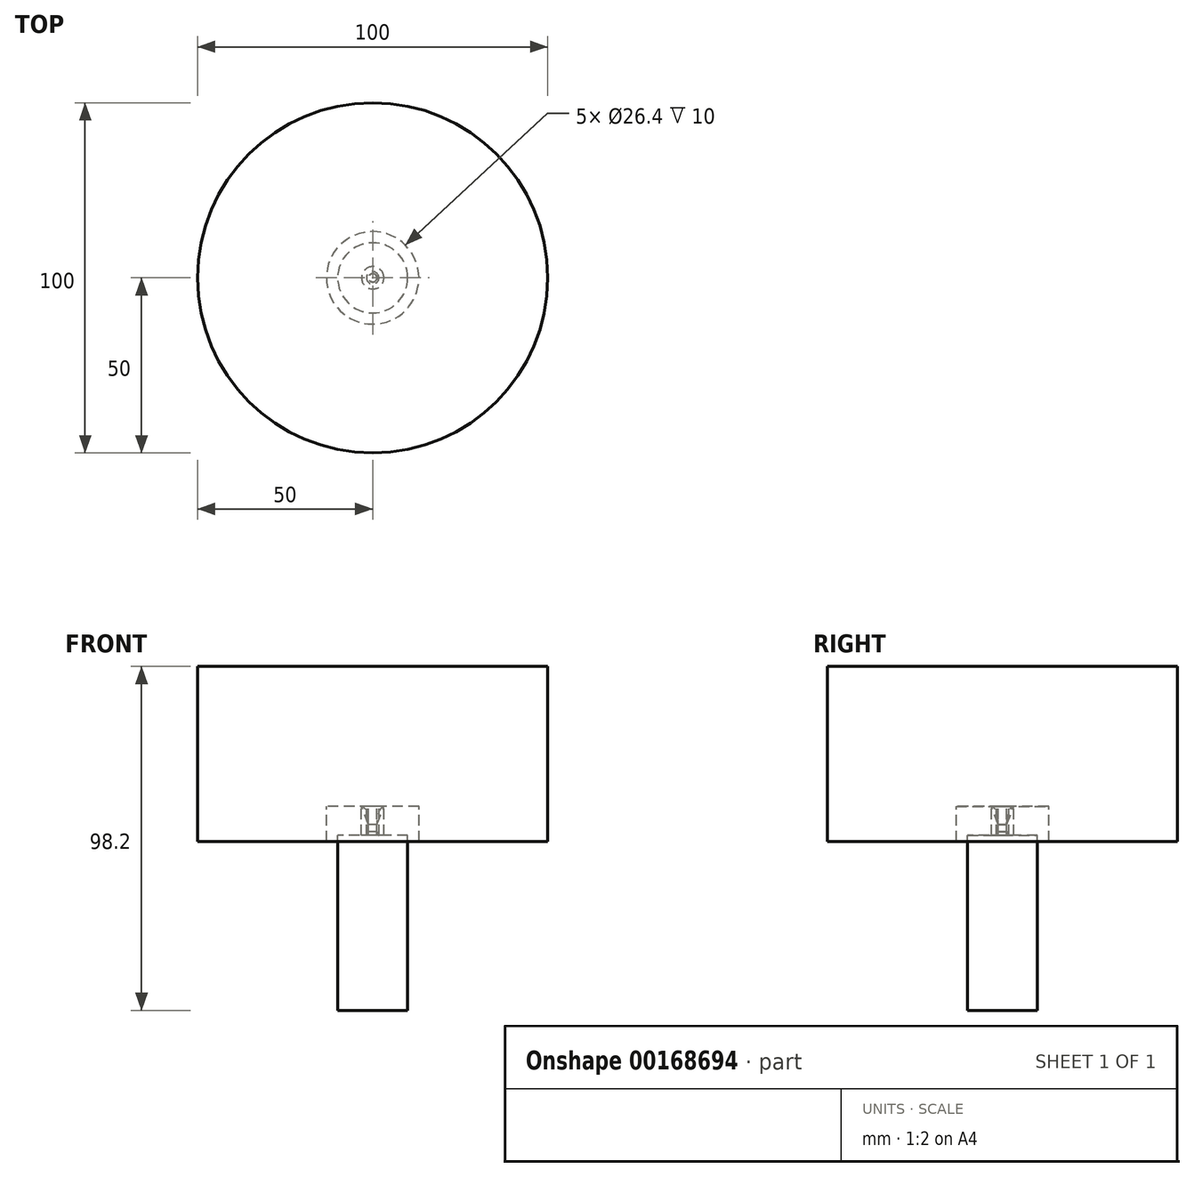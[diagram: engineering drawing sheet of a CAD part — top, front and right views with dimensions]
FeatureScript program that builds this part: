
annotation { "Feature Type Name" : "Feature", "Feature Type Description" : "" }
export const myFeature = defineFeature(function(context is Context, id is Id, definition is map)
    precondition{}
    {
        {
            var Q0;
            Q0=qCreatedBy(makeId("Front.planeOp"),FACE);
            var sketch = newSketch(context, id + "F0", { "sketchPlane" : qUnion([Q0])});
            skLineSegment(sketch, "E0.bottom", {"start": v(0, 0) * mm, "end": v(3.2, 0) * mm, "construction": true});
            skLineSegment(sketch, "E0.top", {"start": v(0, 5.2) * mm, "end": v(3.2, 5.2) * mm, "construction": true});
            skLineSegment(sketch, "E0.left", {"start": v(0, 0) * mm, "end": v(0, 5.2) * mm, "construction": true});
            skLineSegment(sketch, "E0.right", {"start": v(3.2, 0) * mm, "end": v(3.2, 5.2) * mm, "construction": true});
            skLineSegment(sketch, "E1.bottom", {"start": v(0, 0) * mm, "end": v(1.2, 0) * mm, "construction": true});
            skLineSegment(sketch, "E1.top", {"start": v(0, -2) * mm, "end": v(1.2, -2) * mm, "construction": true});
            skLineSegment(sketch, "E1.left", {"start": v(0, 0) * mm, "end": v(0, -2) * mm, "construction": true});
            skLineSegment(sketch, "E1.right", {"start": v(1.2, 0) * mm, "end": v(1.2, -2) * mm, "construction": true});
            skLineSegment(sketch, "E2.bottom", {"start": v(0, -2) * mm, "end": v(1.78, -2) * mm, "construction": true});
            skLineSegment(sketch, "E2.top", {"start": v(0, -3) * mm, "end": v(1.78, -3) * mm, "construction": true});
            skLineSegment(sketch, "E2.left", {"start": v(0, -2) * mm, "end": v(0, -3) * mm, "construction": true});
            skLineSegment(sketch, "E2.right", {"start": v(1.78, -2) * mm, "end": v(1.78, -3) * mm, "construction": true});
            skLineSegment(sketch, "E3", {"start": v(1.2, -2) * mm, "end": v(1.78, -3) * mm, "construction": true});
            skEllipticalArc(sketch, "E4", {});
            skLineSegment(sketch, "E5", {"start": v(3.2, 5.2) * mm, "end": v(13.2, 5.2) * mm});
            skLineSegment(sketch, "E6", {"start": v(13.2, 5.2) * mm, "end": v(13.2, -4.8) * mm});
            skLineSegment(sketch, "E7", {"start": v(13.2, -4.8) * mm, "end": v(50, -4.8) * mm});
            skLineSegment(sketch, "E8", {"start": v(50, -4.8) * mm, "end": v(50, 45.2) * mm});
            skLineSegment(sketch, "E9", {"start": v(50, 45.2) * mm, "end": v(0, 45.2) * mm});
            skLineSegment(sketch, "E10", {"start": v(0, 45.2) * mm, "end": v(0, -53) * mm});
            skLineSegment(sketch, "E11", {"start": v(0, -53) * mm, "end": v(10, -53) * mm});
            skLineSegment(sketch, "E12", {"start": v(10, -53) * mm, "end": v(10, -3) * mm});
            skLineSegment(sketch, "E13", {"start": v(10, -3) * mm, "end": v(1.78, -3) * mm});
            skLineSegment(sketch, "E14", {"start": v(1.2, -2) * mm, "end": v(1.2, 0) * mm});
            skLineSegment(sketch, "E15", {"start": v(1.2, -2) * mm, "end": v(1.78, -3) * mm});
            const initialGuessF0  = {"E4": [0.0032, 0, 0, 1, 0.0052, 0.002, 0, 1.5707963267948966]};
            skSetInitialGuess(sketch, initialGuessF0);
            skSolve(sketch);
        }
        {
            var Q0;
            Q0 = qSketchRegion(id + "F0", true);
            var Q1;
            Q1=sQuery(id+"F0.wireOp",EDGE,"E10");
            revolve(context, id + "F1", {"entities" : qUnion([Q0]), "axis" : qUnion([Q1]), "revolveType" : RevolveType.FULL});
        }
        {
            var Q0;
            Q0=qCreatedBy(makeId("Front.planeOp"),FACE);
            var sketch = newSketch(context, id + "F2", { "sketchPlane" : qUnion([Q0])});
            skEllipticalArc(sketch, "E16.0.0", {"construction": true});
            skLineSegment(sketch, "E16.0.1", {"start": v(3.2, 5.2) * mm, "end": v(13.2, 5.2) * mm});
            skLineSegment(sketch, "E16.0.2", {"start": v(13.2, 5.2) * mm, "end": v(13.2, -4.8) * mm});
            skLineSegment(sketch, "E16.0.3", {"start": v(13.2, -4.8) * mm, "end": v(50, -4.8) * mm});
            skLineSegment(sketch, "E16.0.4", {"start": v(50, -4.8) * mm, "end": v(50, 45.2) * mm});
            skLineSegment(sketch, "E16.0.5", {"start": v(50, 45.2) * mm, "end": v(0, 45.2) * mm});
            skLineSegment(sketch, "E16.0.6", {"start": v(0, 45.2) * mm, "end": v(0, -53) * mm});
            skLineSegment(sketch, "E16.0.7", {"start": v(0, -53) * mm, "end": v(10, -53) * mm});
            skLineSegment(sketch, "E16.0.8", {"start": v(10, -53) * mm, "end": v(10, -3) * mm});
            skLineSegment(sketch, "E16.0.9", {"start": v(10, -3) * mm, "end": v(1.78, -3) * mm});
            skLineSegment(sketch, "E16.0.10", {"start": v(1.78, -3) * mm, "end": v(1.2, -2) * mm, "construction": true});
            skLineSegment(sketch, "E16.0.11", {"start": v(1.2, -2) * mm, "end": v(1.2, 0) * mm});
            skLineSegment(sketch, "E17", {"start": v(3.2, 5.2) * mm, "end": v(1.2, 5.2) * mm});
            skLineSegment(sketch, "E18", {"start": v(1.2, 5.2) * mm, "end": v(1.2, 0) * mm});
            skLineSegment(sketch, "E19", {"start": v(1.2, -2) * mm, "end": v(1.2, -3) * mm});
            skLineSegment(sketch, "E20", {"start": v(1.2, -3) * mm, "end": v(1.78, -3) * mm});
            const initialGuessF2  = {"E16.0.0": [0.0032, 0, 0, 1, 0.0052, 0.002, 0, 1.5707963267948966]};
            skSetInitialGuess(sketch, initialGuessF2);
            skSolve(sketch);
        }
        {
            var Q0;
            Q0 = qSketchRegion(id + "F2", true);
            var Q1;
            Q1=sQuery(id+"F2.wireOp",EDGE,"E16.0.6");
            revolve(context, id + "F3", {"entities" : qUnion([Q0]), "axis" : qUnion([Q1]), "revolveType" : RevolveType.FULL});
        }
        {
            var Q0;
            Q0=qCreatedBy(makeId("Front.planeOp"),FACE);
            var sketch = newSketch(context, id + "F4", { "sketchPlane" : qUnion([Q0])});
            skLineSegment(sketch, "E21.0.0", {"start": v(1.2, 5.2) * mm, "end": v(3.2, 5.2) * mm, "construction": true});
            skLineSegment(sketch, "E21.0.1", {"start": v(3.2, 5.2) * mm, "end": v(13.2, 5.2) * mm, "construction": true});
            skLineSegment(sketch, "E21.0.2", {"start": v(13.2, 5.2) * mm, "end": v(13.2, -4.8) * mm, "construction": true});
            skLineSegment(sketch, "E21.0.3", {"start": v(13.2, -4.8) * mm, "end": v(50, -4.8) * mm});
            skLineSegment(sketch, "E21.0.4", {"start": v(50, -4.8) * mm, "end": v(50, 45.2) * mm});
            skLineSegment(sketch, "E21.0.5", {"start": v(50, 45.2) * mm, "end": v(0, 45.2) * mm});
            skLineSegment(sketch, "E21.0.6", {"start": v(0, 45.2) * mm, "end": v(0, -53) * mm});
            skLineSegment(sketch, "E21.0.7", {"start": v(0, -53) * mm, "end": v(10, -53) * mm});
            skLineSegment(sketch, "E21.0.8", {"start": v(10, -53) * mm, "end": v(10, -3) * mm});
            skLineSegment(sketch, "E21.0.9", {"start": v(10, -3) * mm, "end": v(1.78, -3) * mm, "construction": true});
            skLineSegment(sketch, "E21.0.10", {"start": v(1.78, -3) * mm, "end": v(1.2, -3) * mm, "construction": true});
            skLineSegment(sketch, "E21.0.11", {"start": v(1.2, -3) * mm, "end": v(1.2, -2) * mm, "construction": true});
            skLineSegment(sketch, "E21.0.12", {"start": v(1.2, -2) * mm, "end": v(1.2, 0) * mm, "construction": true});
            skLineSegment(sketch, "E21.0.13", {"start": v(1.2, 0) * mm, "end": v(1.2, 5.2) * mm, "construction": true});
            skLineSegment(sketch, "E22", {"start": v(10, -3) * mm, "end": v(1.78, -3) * mm});
            skLineSegment(sketch, "E23", {"start": v(1.78, 5.2) * mm, "end": v(13.2, 5.2) * mm});
            skLineSegment(sketch, "E24", {"start": v(13.2, -4.8) * mm, "end": v(13.2, 5.2) * mm});
            skLineSegment(sketch, "E25", {"start": v(1.78, -3) * mm, "end": v(1.78, 5.2) * mm});
            skSolve(sketch);
        }
        {
            var Q0;
            Q0 = qSketchRegion(id + "F4", true);
            var Q1;
            Q1 = qConstructionFilter(qBodyType(qCreatedBy(id + "F4" ,EDGE), BodyType.WIRE), ConstructionObject.NO);
            var Q2;
            Q2=sQuery(id+"F4.wireOp",EDGE,"E21.0.6");
            revolve(context, id + "F5", {"entities" : qUnion([Q0]), "surfaceEntities" : qUnion([Q1]), "axis" : qUnion([Q2]), "revolveType" : RevolveType.FULL});
        }
        {
            var Q0;
            Q0=qCreatedBy(makeId("Front.planeOp"),FACE);
            var sketch = newSketch(context, id + "F6", { "sketchPlane" : qUnion([Q0])});
            skLineSegment(sketch, "E26.0.0", {"start": v(13.2, 5.2) * mm, "end": v(13.2, -4.8) * mm});
            skLineSegment(sketch, "E26.0.1", {"start": v(13.2, -4.8) * mm, "end": v(50, -4.8) * mm});
            skLineSegment(sketch, "E26.0.2", {"start": v(50, -4.8) * mm, "end": v(50, 45.2) * mm});
            skLineSegment(sketch, "E26.0.3", {"start": v(50, 45.2) * mm, "end": v(0, 45.2) * mm});
            skLineSegment(sketch, "E26.0.4", {"start": v(0, 45.2) * mm, "end": v(0, -53) * mm});
            skLineSegment(sketch, "E26.0.5", {"start": v(0, -53) * mm, "end": v(10, -53) * mm});
            skLineSegment(sketch, "E26.0.6", {"start": v(10, -53) * mm, "end": v(10, -3) * mm});
            skLineSegment(sketch, "E26.0.7", {"start": v(10, -3) * mm, "end": v(3.2, -3) * mm});
            skLineSegment(sketch, "E26.0.8", {"start": v(3.2, -3) * mm, "end": v(3.2, 5.2) * mm});
            skLineSegment(sketch, "E26.0.9", {"start": v(3.2, 5.2) * mm, "end": v(13.2, 5.2) * mm});
            skPoint(sketch, "E27.0", {"position": v(3.2, 5.2) * mm});
            skSolve(sketch);
        }
        {
            var Q0;
            Q0 = qSketchRegion(id + "F6", true);
            var Q1;
            Q1=sQuery(id+"F6.wireOp",EDGE,"E26.0.4");
            revolve(context, id + "F7", {"entities" : qUnion([Q0]), "axis" : qUnion([Q1]), "revolveType" : RevolveType.FULL});
        }
        {
            var Q0;
            Q0=makeQuery(id+"F0.imprint","IMPRINT",FACE,{"disambiguationData":[TD([[makeQuery(id+"F0.imprint","IMPRINT",EDGE,{"derivedFrom":sQuery(id+"F0.wireOp",EDGE,"E4")}),-1.0]])]});
            var sketch = newSketch(context, id + "F8", { "sketchPlane" : qUnion([Q0])});
            skLineSegment(sketch, "E28.0.1", {"start": v(3.2, 5.2) * mm, "end": v(13.2, 5.2) * mm});
            skLineSegment(sketch, "E28.0.2", {"start": v(13.2, 5.2) * mm, "end": v(13.2, -4.8) * mm});
            skLineSegment(sketch, "E28.0.3", {"start": v(13.2, -4.8) * mm, "end": v(50, -4.8) * mm});
            skLineSegment(sketch, "E28.0.4", {"start": v(50, -4.8) * mm, "end": v(50, 45.2) * mm});
            skLineSegment(sketch, "E28.0.5", {"start": v(50, 45.2) * mm, "end": v(0, 45.2) * mm});
            skLineSegment(sketch, "E28.0.6", {"start": v(0, 45.2) * mm, "end": v(0, -53) * mm});
            skLineSegment(sketch, "E28.0.7", {"start": v(0, -53) * mm, "end": v(10, -53) * mm});
            skLineSegment(sketch, "E28.0.8", {"start": v(10, -53) * mm, "end": v(10, -3) * mm});
            skLineSegment(sketch, "E28.0.9", {"start": v(10, -3) * mm, "end": v(1.78, -3) * mm});
            skLineSegment(sketch, "E28.0.10", {"start": v(1.78, -3) * mm, "end": v(1.2, -2) * mm});
            skLineSegment(sketch, "E28.0.11", {"start": v(1.2, -2) * mm, "end": v(1.2, 0) * mm});
            skLineSegment(sketch, "E29", {"start": v(3.2, 5.2) * mm, "end": v(1.2, 0) * mm});
            skSolve(sketch);
        }
        {
            var Q0;
            Q0 = qSketchRegion(id + "F8", true);
            var Q1;
            Q1=sQuery(id+"F8.wireOp",EDGE,"E28.0.6");
            revolve(context, id + "F9", {"entities" : qUnion([Q0]), "axis" : qUnion([Q1]), "revolveType" : RevolveType.FULL});
        }
    });
